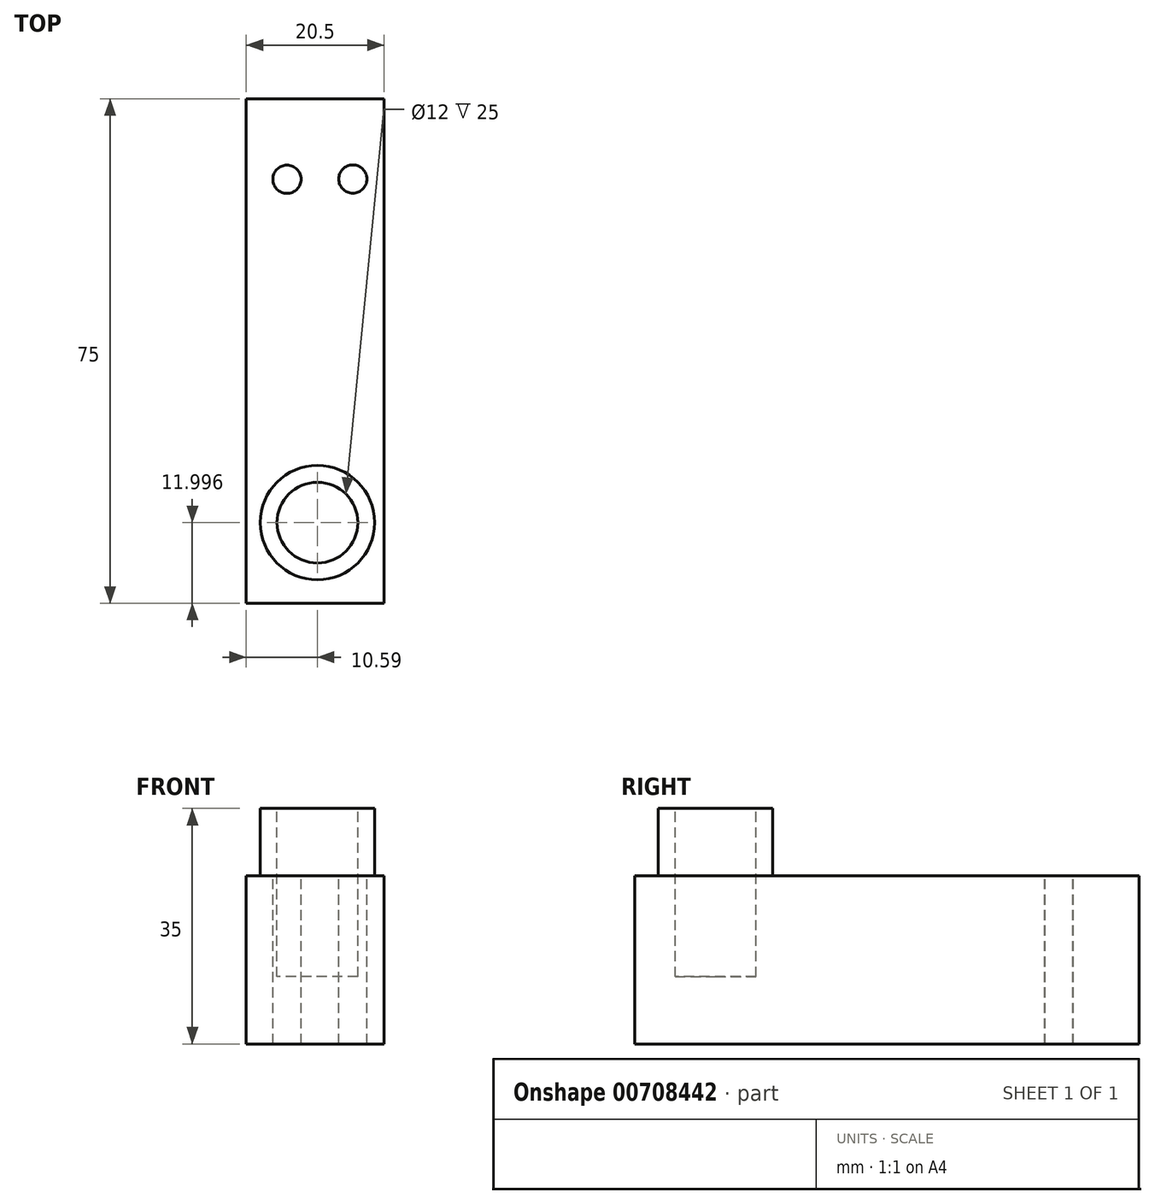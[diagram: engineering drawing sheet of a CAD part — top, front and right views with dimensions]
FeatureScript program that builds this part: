
annotation { "Feature Type Name" : "Feature", "Feature Type Description" : "" }
export const myFeature = defineFeature(function(context is Context, id is Id, definition is map)
    precondition{}
    {
        {
            var Q0;
            Q0=qCreatedBy(makeId("Top.planeOp"),FACE);
            var sketch = newSketch(context, id + "F0", { "sketchPlane" : qUnion([Q0])});
            skLineSegment(sketch, "E0.bottom", {"start": v(-10.6, 51.98) * mm, "end": v(9.9, 51.98) * mm});
            skLineSegment(sketch, "E0.top", {"start": v(-10.6, -23.02) * mm, "end": v(9.9, -23.02) * mm});
            skLineSegment(sketch, "E0.left", {"start": v(-10.6, 51.98) * mm, "end": v(-10.6, -23.02) * mm});
            skLineSegment(sketch, "E0.right", {"start": v(9.9, 51.98) * mm, "end": v(9.9, -23.02) * mm});
            skSolve(sketch);
        }
        {
            var Q0;
            Q0=qSketchRegion(id+"F0",true);
            extrude(context, id + "F1", {"entities" : qUnion([Q0]), "depth" : 25 * mm, "offsetDistance" : 25 * mm});
        }
        {
            var Q0;
            Q0=makeQuery(id+"F1.opExtrude","CAP_FACE",FACE,{"disambiguationData":[OSD([sQuery(id+"F0.wireOp",EDGE,"E0.bottom"),sQuery(id+"F0.wireOp",EDGE,"E0.top"),sQuery(id+"F0.wireOp",EDGE,"E0.left"),sQuery(id+"F0.wireOp",EDGE,"E0.right")])],"isStart":false});
            var sketch = newSketch(context, id + "F2", { "sketchPlane" : qUnion([Q0])});
            skCircle(sketch, "E1", {"center": v(0, -11.02) * mm, "radius": 8.5 * mm});
            skSolve(sketch);
        }
        {
            var Q0;
            Q0=qSketchRegion(id+"F2",true);
            extrude(context, id + "F3", {"entities" : qUnion([Q0]), "operationType" : NewBodyOperationType.ADD, "depth" : 10 * mm, "offsetDistance" : 25 * mm});
        }
        {
            var Q0;
            Q0=makeQuery(id+"F1.opExtrude","CAP_FACE",FACE,{"disambiguationData":[OSD([sQuery(id+"F0.wireOp",EDGE,"E0.bottom"),sQuery(id+"F0.wireOp",EDGE,"E0.top"),sQuery(id+"F0.wireOp",EDGE,"E0.left"),sQuery(id+"F0.wireOp",EDGE,"E0.right")])],"isStart":false});
            var sketch = newSketch(context, id + "F4", { "sketchPlane" : qUnion([Q0])});
            skCircle(sketch, "E2", {"center": v(-4.53, 40.03) * mm, "radius": 2.5 * mm});
            skCircle(sketch, "E3", {"center": v(5.27, 40.06) * mm, "radius": 2.37 * mm});
            skSolve(sketch);
        }
        {
            var Q0;
            Q0=sQuery(id+"F4.wireOp",VERTEX,"E2.center");
            var Q1;
            Q1=sQuery(id+"F4.wireOp",VERTEX,"E3.center");
            var Q2;
            Q2=makeQuery(id+"F1.opExtrude","SWEPT_BODY",BODY,{"disambiguationData":[OSD([sQuery(id+"F0.wireOp",EDGE,"E0.bottom"),sQuery(id+"F0.wireOp",EDGE,"E0.top"),sQuery(id+"F0.wireOp",EDGE,"E0.left"),sQuery(id+"F0.wireOp",EDGE,"E0.right")])]});
            hole(context, id + "F5", {"style" : HoleStyle.SIMPLE, "endStyle" : HoleEndStyle.THROUGH, "standardTappedOrClearance" : lookupTablePath({ "standard" : "ISO", "engagement" : "75%", "pitch" : "0.8 mm", "size" : "M5", "type" : "Tapped" }), "standardBlindInLast" : lookupTablePath({ "standard" : "ISO", "engagement" : "75%", "pitch" : "0.8 mm", "size" : "M5", "type" : "Tapped" }), "holeDiameter" : 4.2 * mm, "majorDiameter" : 5 * mm, "showTappedDepth" : true, "isTappedThrough" : true, "tappedDepth" : 12 * mm, "tapClearance" : 3, "locations" : qUnion([Q0, Q1]), "scope" : qUnion([Q2])});
        }
        {
            var Q0;
            Q0=makeQuery(id+"F3.opExtrude","CAP_FACE",FACE,{"disambiguationData":[OSD([sQuery(id+"F2.wireOp",EDGE,"E1")])],"isStart":false});
            var sketch = newSketch(context, id + "F6", { "sketchPlane" : qUnion([Q0])});
            skCircle(sketch, "E4", {"center": v(0, -11.02) * mm, "radius": 6 * mm});
            skSolve(sketch);
        }
        {
            var Q0;
            Q0=makeQuery(id+"F6.imprint","IMPRINT",FACE,{"disambiguationData":[TD([[makeQuery(id+"F6.imprint","IMPRINT",EDGE,{"derivedFrom":sQuery(id+"F6.wireOp",EDGE,"E4")}),1.0]])]});
            extrude(context, id + "F7", {"entities" : qUnion([Q0]), "operationType" : NewBodyOperationType.REMOVE, "oppositeDirection" : true, "depth" : 25 * mm, "offsetDistance" : 25 * mm});
        }
    });
